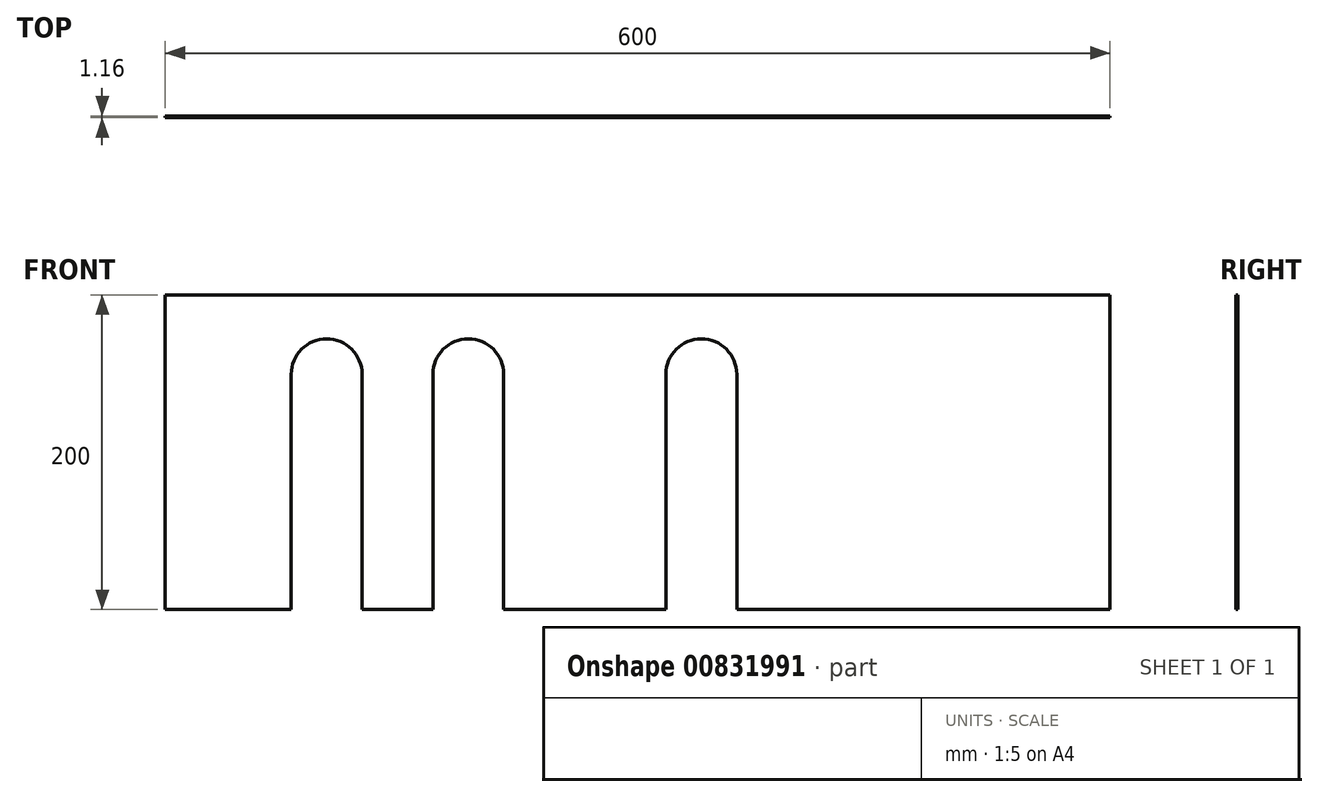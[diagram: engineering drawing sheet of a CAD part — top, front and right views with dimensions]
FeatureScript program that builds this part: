
annotation { "Feature Type Name" : "Feature", "Feature Type Description" : "" }
export const myFeature = defineFeature(function(context is Context, id is Id, definition is map)
    precondition{}
    {
        {
            var Q0;
            Q0=qCreatedBy(makeId("Front.planeOp"),FACE);
            var sketch = newSketch(context, id + "F0", { "sketchPlane" : qUnion([Q0])});
            skLineSegment(sketch, "E0", {"start": v(0, 0) * mm, "end": v(0, 200) * mm});
            skLineSegment(sketch, "E1", {"start": v(0, 200) * mm, "end": v(600, 200) * mm});
            skLineSegment(sketch, "E2", {"start": v(600, 200) * mm, "end": v(600, 0) * mm});
            skLineSegment(sketch, "E3", {"start": v(0, 0) * mm, "end": v(80, 0) * mm});
            skLineSegment(sketch, "E4", {"start": v(80, 0) * mm, "end": v(125, 0) * mm, "construction": true});
            skLineSegment(sketch, "E5", {"start": v(125, 0) * mm, "end": v(170, 0) * mm});
            skLineSegment(sketch, "E6", {"start": v(170, 0) * mm, "end": v(215, 0) * mm, "construction": true});
            skLineSegment(sketch, "E7", {"start": v(215, 0) * mm, "end": v(318, 0) * mm});
            skLineSegment(sketch, "E8", {"start": v(318, 0) * mm, "end": v(363, 0) * mm, "construction": true});
            skLineSegment(sketch, "E9", {"start": v(363, 0) * mm, "end": v(600, 0) * mm});
            skLineSegment(sketch, "E10", {"start": v(80, 0) * mm, "end": v(80, 149.5) * mm});
            skLineSegment(sketch, "E11", {"start": v(125, 0) * mm, "end": v(125, 149.5) * mm});
            skLineSegment(sketch, "E12", {"start": v(170, 0) * mm, "end": v(170, 149.5) * mm});
            skLineSegment(sketch, "E13", {"start": v(215, 0) * mm, "end": v(215, 149.5) * mm});
            skLineSegment(sketch, "E14", {"start": v(318, 0) * mm, "end": v(318, 149.5) * mm});
            skLineSegment(sketch, "E15", {"start": v(363, 0) * mm, "end": v(363, 149.5) * mm});
            skLineSegment(sketch, "E16", {"start": v(0, 149.5) * mm, "end": v(600, 149.5) * mm, "construction": true});
            skArc(sketch, "E17", {"start": v(125, 149.5) * mm, "mid": v(102.5, 172) * mm, "end": v(80, 149.5) * mm});
            skArc(sketch, "E18", {"start": v(215, 149.5) * mm, "mid": v(192.5, 172) * mm, "end": v(170, 149.5) * mm});
            skArc(sketch, "E19", {"start": v(363, 149.5) * mm, "mid": v(340.5, 172) * mm, "end": v(318, 149.5) * mm});
            skPoint(sketch, "E20", {"position": v(102.5, 172) * mm});
            skPoint(sketch, "E21", {"position": v(192.5, 172) * mm});
            skPoint(sketch, "E22", {"position": v(340.5, 172) * mm});
            skLineSegment(sketch, "E23", {"start": v(102.5, 172) * mm, "end": v(340.5, 172) * mm, "construction": true});
            skSolve(sketch);
        }
        {
            var Q0;
            Q0 = qSketchRegion(id + "F0", true);
            extrude(context, id + "F1", {"entities" : qUnion([Q0]), "depth" : 1.16 * mm, "offsetDistance" : 25 * mm});
        }
    });
